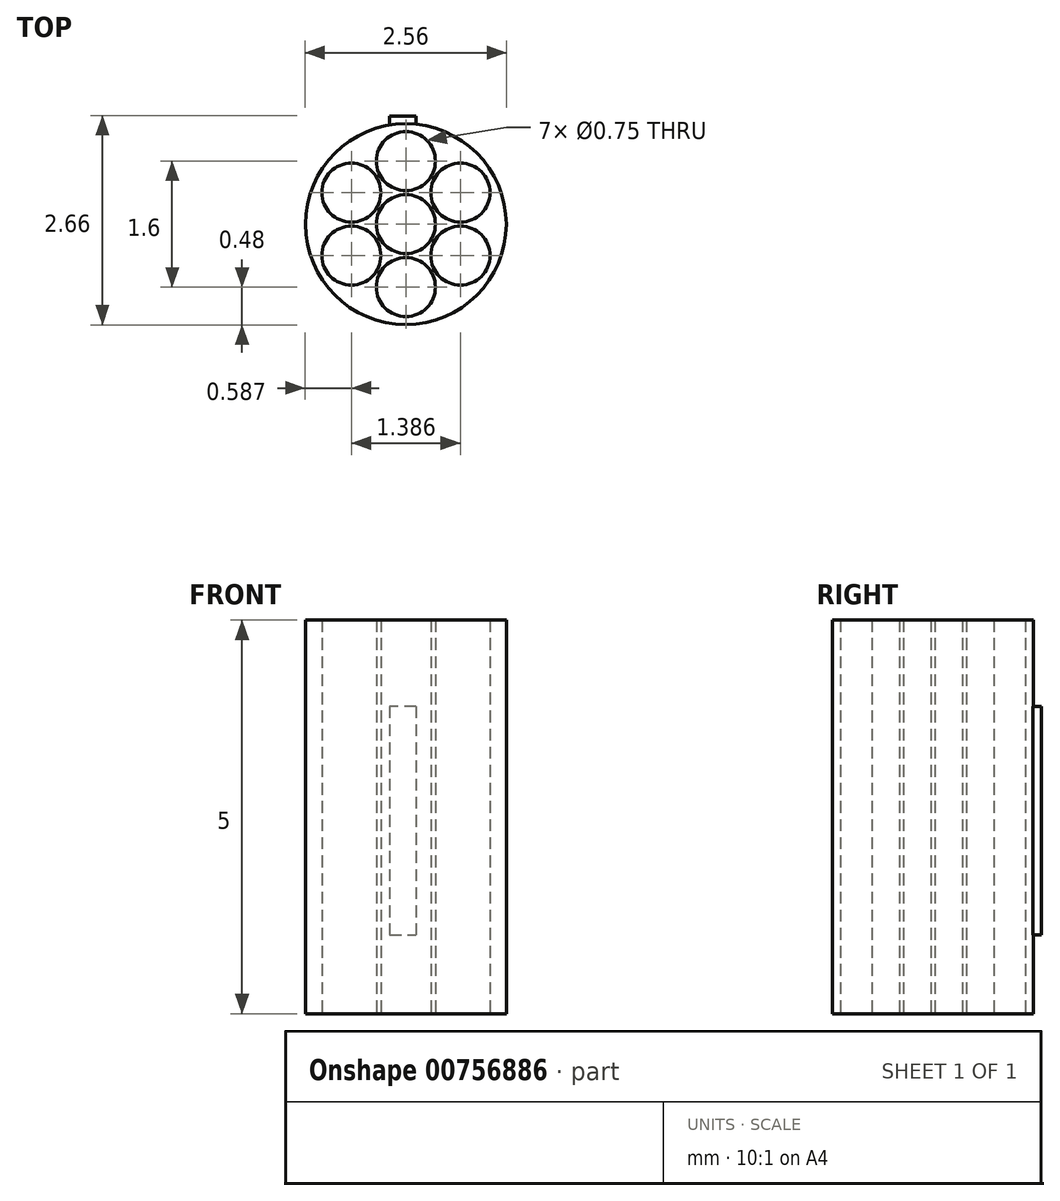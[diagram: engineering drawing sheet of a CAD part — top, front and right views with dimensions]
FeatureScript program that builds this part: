
annotation { "Feature Type Name" : "Feature", "Feature Type Description" : "" }
export const myFeature = defineFeature(function(context is Context, id is Id, definition is map)
    precondition{}
    {
        {
            var Q0;
            Q0=qCreatedBy(makeId("Top.planeOp"),FACE);
            var sketch = newSketch(context, id + "F0", { "sketchPlane" : qUnion([Q0])});
            skCircle(sketch, "E0", {"center": v(0, 0) * mm, "radius": 0.8 * mm});
            skCircle(sketch, "E1.cCircle", {"center": v(0, 0) * mm, "radius": 0.8 * mm, "construction": true});
            skLineSegment(sketch, "E1.0", {"start": v(0, 0.8) * mm, "end": v(0.7, 0.4) * mm});
            skLineSegment(sketch, "E1.1", {"start": v(0.7, 0.4) * mm, "end": v(0.7, -0.4) * mm});
            skLineSegment(sketch, "E1.2", {"start": v(0.7, -0.4) * mm, "end": v(0, -0.8) * mm});
            skLineSegment(sketch, "E1.3", {"start": v(0, -0.8) * mm, "end": v(-0.7, -0.4) * mm});
            skLineSegment(sketch, "E1.4", {"start": v(-0.7, -0.4) * mm, "end": v(-0.7, 0.4) * mm});
            skLineSegment(sketch, "E1.5", {"start": v(-0.7, 0.4) * mm, "end": v(0, 0.8) * mm});
            skSolve(sketch);
        }
        {
            var Q0;
            Q0=qCreatedBy(makeId("Top.planeOp"),FACE);
            var sketch = newSketch(context, id + "F1", { "sketchPlane" : qUnion([Q0])});
            skCircle(sketch, "E2", {"center": v(0, 0) * mm, "radius": 0.38 * mm});
            skCircle(sketch, "E3", {"center": v(0, 0.8) * mm, "radius": 0.38 * mm});
            skCircle(sketch, "E4", {"center": v(0.7, 0.4) * mm, "radius": 0.38 * mm});
            skCircle(sketch, "E5", {"center": v(0.7, -0.4) * mm, "radius": 0.38 * mm});
            skCircle(sketch, "E6", {"center": v(0, -0.8) * mm, "radius": 0.38 * mm});
            skCircle(sketch, "E7", {"center": v(-0.7, -0.4) * mm, "radius": 0.38 * mm});
            skCircle(sketch, "E8", {"center": v(-0.7, 0.4) * mm, "radius": 0.38 * mm});
            skSolve(sketch);
        }
        {
            var Q0;
            Q0=qCreatedBy(makeId("Top.planeOp"),FACE);
            var sketch = newSketch(context, id + "F2", { "sketchPlane" : qUnion([Q0])});
            skCircle(sketch, "E9", {"center": v(0, 0) * mm, "radius": 1.27 * mm});
            skSolve(sketch);
        }
        {
            var Q0;
            Q0=qSketchRegion(id+"F2",true);
            extrude(context, id + "F3", {"entities" : qUnion([Q0]), "depth" : 5 * mm, "offsetDistance" : 25 * mm});
        }
        {
            var Q0;
            Q0=qSketchRegion(id+"F1",true);
            extrude(context, id + "F4", {"entities" : qUnion([Q0]), "operationType" : NewBodyOperationType.REMOVE, "endBound" : BoundingType.THROUGH_ALL, "depth" : 25 * mm, "offsetDistance" : 25 * mm});
        }
        {
            var Q0;
            Q0=makeQuery(id+"F3.opExtrude","CAP_FACE",FACE,{"disambiguationData":[OSD([sQuery(id+"F2.wireOp",EDGE,"E9")])],"isStart":false});
            var sketch = newSketch(context, id + "F5", { "sketchPlane" : qUnion([Q0])});
            skPoint(sketch, "E10", {"position": v(0, -1.27) * mm});
            skPoint(sketch, "E11", {"position": v(-0.36, -1.27) * mm});
            skPoint(sketch, "E12", {"position": v(0.42, -1.27) * mm});
            skSolve(sketch);
        }
        {
            var Q0;
            Q0=makeQuery(id+"F3.opExtrude","CAP_FACE",FACE,{"disambiguationData":[OSD([sQuery(id+"F2.wireOp",EDGE,"E9")])],"isStart":true});
            var sketch = newSketch(context, id + "F6", { "sketchPlane" : qUnion([Q0])});
            skPoint(sketch, "E13", {"position": v(0, 1.27) * mm});
            skPoint(sketch, "E14", {"position": v(-0.36, 1.27) * mm});
            skPoint(sketch, "E15", {"position": v(0.42, 1.27) * mm});
            skSolve(sketch);
        }
        {
            var Q0;
            Q0=sQuery(id+"F5.wireOp",VERTEX,"E10");
            var Q1;
            Q1=sQuery(id+"F6.wireOp",VERTEX,"E13");
            var Q2;
            Q2=sQuery(id+"F6.wireOp",VERTEX,"E15");
            cPlane(context, id + "F7", {"entities" : qUnion([Q0, Q1, Q2]), "cplaneType" : CPlaneType.THREE_POINT, "offset" : 0 * mm, "oppositeDirection" : true, "width" : 150 * mm, "height" : 150 * mm});
        }
        {
            var Q0;
            Q0=qCreatedBy(id+"F7.planeOp",FACE);
            cPlane(context, id + "F8", {"entities" : qUnion([Q0]), "cplaneType" : CPlaneType.OFFSET, "offset" : 2.45 * mm, "width" : 150 * mm, "height" : 150 * mm});
        }
        {
            var Q0;
            Q0=qCreatedBy(id+"F8.planeOp",FACE);
            var sketch = newSketch(context, id + "F9", { "sketchPlane" : qUnion([Q0])});
            skText(sketch, "E16", { "text": "I", "fontName": "OpenSans-Regular.ttf"});
            const initialGuessF9  = {"E16": [-0.00053, 0.001, 1, 0, 0.00293]};
            skSetInitialGuess(sketch, initialGuessF9);
            skSolve(sketch);
        }
        {
            var Q0;
            Q0 = qSketchRegion(id + "F9", true);
            extrude(context, id + "F10", {"entities" : qUnion([Q0]), "operationType" : NewBodyOperationType.ADD, "depth" : 0.2 * mm, "offsetDistance" : 25 * mm});
        }
    });
